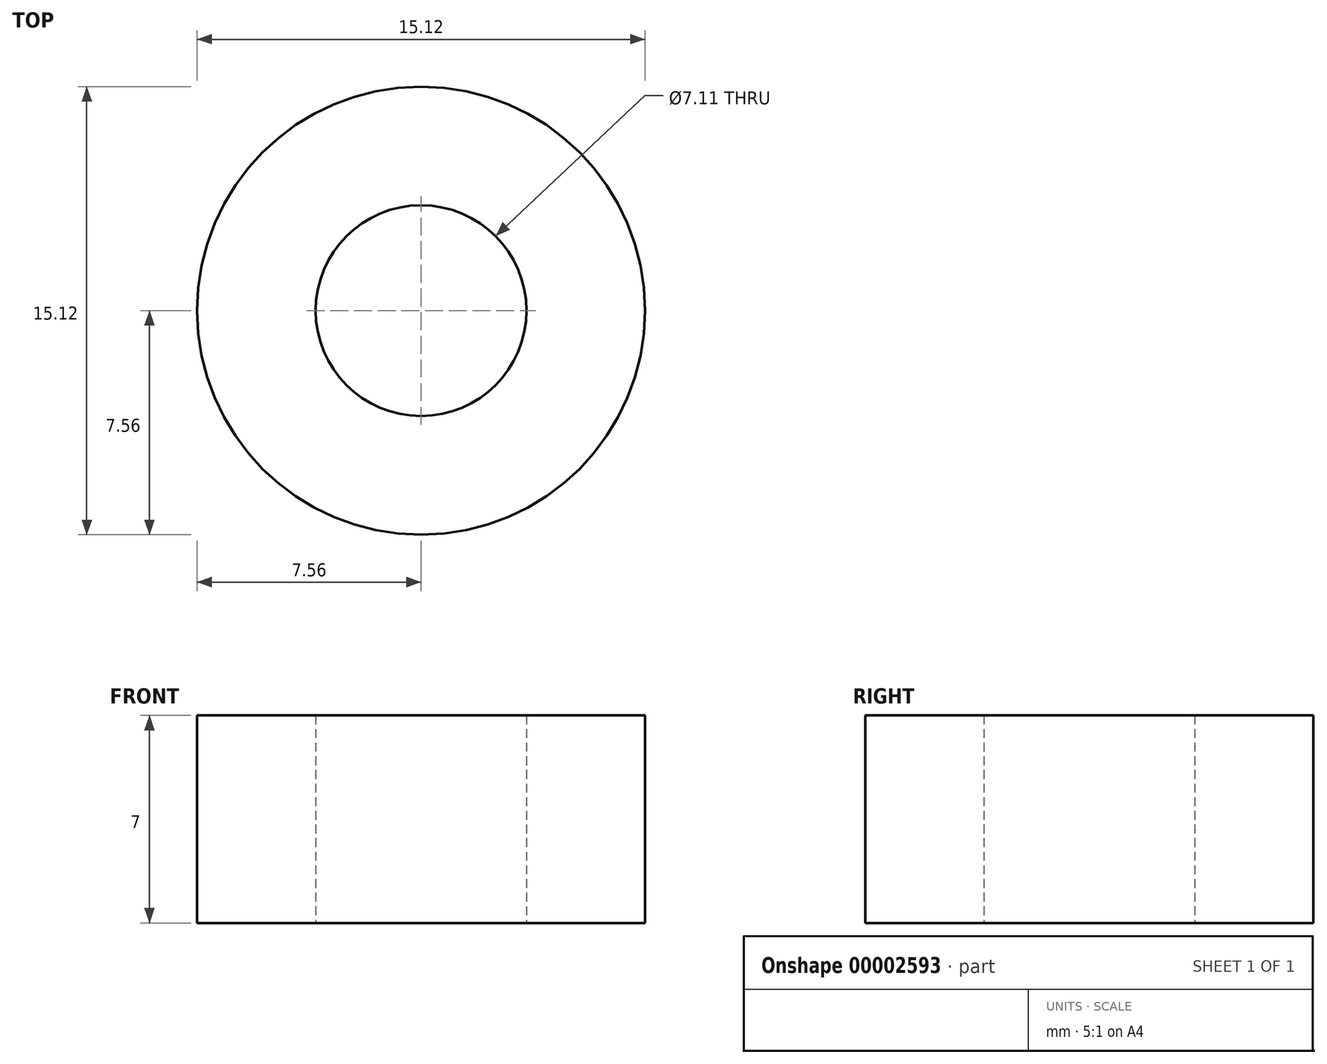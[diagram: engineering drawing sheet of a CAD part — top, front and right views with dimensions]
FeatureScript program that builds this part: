
annotation { "Feature Type Name" : "Feature", "Feature Type Description" : "" }
export const myFeature = defineFeature(function(context is Context, id is Id, definition is map)
    precondition{}
    {
        {
            var Q0;
            Q0=qCreatedBy(makeId("Top.planeOp"),FACE);
            var sketch = newSketch(context, id + "F0", { "sketchPlane" : qUnion([Q0])});
            skCircle(sketch, "E0", {"center": v(0, 0) * mm, "radius": 3.56 * mm});
            skCircle(sketch, "E1.0", {"center": v(0, 0) * mm, "radius": 7.56 * mm});
            skSolve(sketch);
        }
        {
            var Q0;
            Q0=makeQuery(id+"F0.imprint","IMPRINT",FACE,{"disambiguationData":[TD([[makeQuery(id+"F0.imprint","IMPRINT",EDGE,{"derivedFrom":sQuery(id+"F0.wireOp",EDGE,"E0")}),-1.0]])]});
            extrude(context, id + "F1", {"entities" : qUnion([Q0]), "depth" : 7 * mm});
        }
    });
